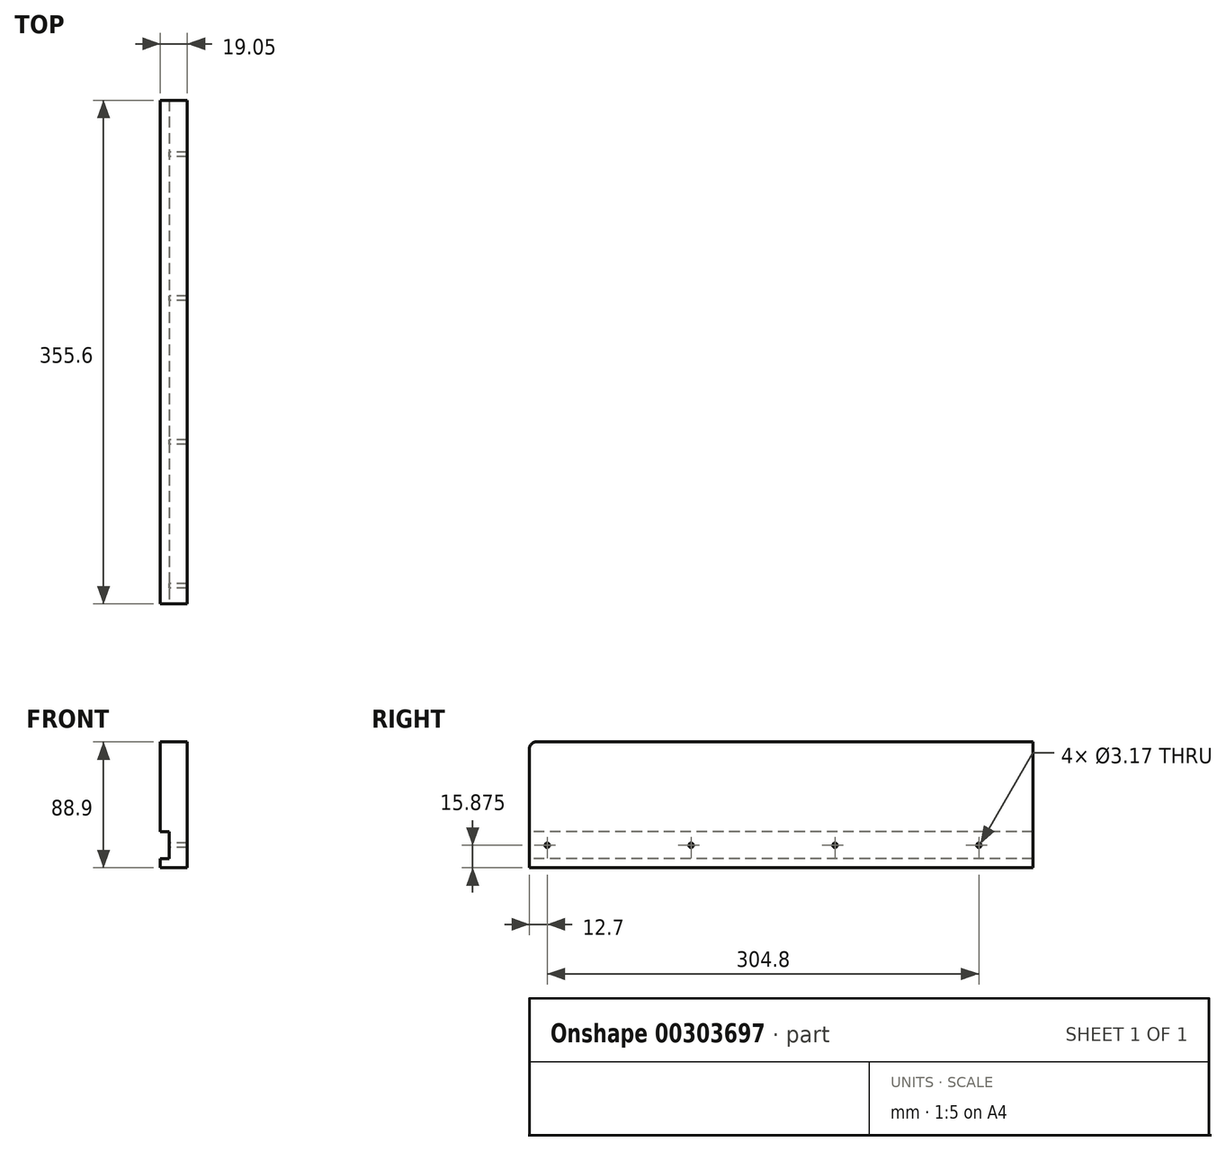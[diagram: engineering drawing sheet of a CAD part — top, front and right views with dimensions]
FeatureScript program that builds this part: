
annotation { "Feature Type Name" : "Feature", "Feature Type Description" : "" }
export const myFeature = defineFeature(function(context is Context, id is Id, definition is map)
    precondition{}
    {
        {
            var Q0;
            Q0=qCreatedBy(makeId("Right.planeOp"),FACE);
            var sketch = newSketch(context, id + "F0", { "sketchPlane" : qUnion([Q0])});
            skLineSegment(sketch, "E0.bottom", {"start": v(0, 0) * mm, "end": v(355.6, 0) * mm});
            skLineSegment(sketch, "E0.top", {"start": v(0, -88.9) * mm, "end": v(355.6, -88.9) * mm});
            skLineSegment(sketch, "E0.left", {"start": v(0, 0) * mm, "end": v(0, -88.9) * mm});
            skLineSegment(sketch, "E0.right", {"start": v(355.6, 0) * mm, "end": v(355.6, -88.9) * mm});
            skSolve(sketch);
        }
        {
            var Q0;
            Q0 = qSketchRegion(id + "F0", true);
            extrude(context, id + "F1", {"entities" : qUnion([Q0]), "depth" : 19.05 * mm});
        }
        {
            var Q0;
            Q0=makeQuery(id+"F1.opExtrude","SWEPT_EDGE",EDGE,{"disambiguationData":[OSD([sQuery(id+"F0.wireOp",EDGE,"E0.bottom"),sQuery(id+"F0.wireOp",EDGE,"E0.left")])]});
            fillet(context, id + "F2", {"entities" : qUnion([Q0]), "radius" : 5.08 * mm, "tangentPropagation" : true, "allowEdgeOverflow" : false});
        }
        {
            var Q0;
            Q0=qCreatedBy(makeId("Right.planeOp"),FACE);
            var sketch = newSketch(context, id + "F3", { "sketchPlane" : qUnion([Q0])});
            skLineSegment(sketch, "E1.bottom", {"start": v(355.6, -63.5) * mm, "end": v(0, -63.5) * mm});
            skLineSegment(sketch, "E1.top", {"start": v(355.6, -82.55) * mm, "end": v(0, -82.55) * mm});
            skLineSegment(sketch, "E1.left", {"start": v(355.6, -63.5) * mm, "end": v(355.6, -82.55) * mm});
            skLineSegment(sketch, "E1.right", {"start": v(0, -63.5) * mm, "end": v(0, -82.55) * mm});
            skSolve(sketch);
        }
        {
            var Q0;
            Q0 = qSketchRegion(id + "F3", true);
            extrude(context, id + "F4", {"entities" : qUnion([Q0]), "operationType" : NewBodyOperationType.REMOVE, "depth" : 6.35 * mm});
        }
        {
            var Q0;
            Q0=qCreatedBy(makeId("Right.planeOp"),FACE);
            var sketch = newSketch(context, id + "F5", { "sketchPlane" : qUnion([Q0])});
            skCircle(sketch, "E2", {"center": v(12.7, -73.03) * mm, "radius": 1.59 * mm});
            skCircle(sketch, "E3.1.0.0", {"center": v(114.3, -73.03) * mm, "radius": 1.59 * mm});
            skCircle(sketch, "E3.2.0.0", {"center": v(215.9, -73.03) * mm, "radius": 1.59 * mm});
            skCircle(sketch, "E3.3.0.0", {"center": v(317.5, -73.03) * mm, "radius": 1.59 * mm});
            skLineSegment(sketch, "E3.direction1", {"start": v(12.7, -73.03) * mm, "end": v(114.3, -73.03) * mm, "construction": true});
            skSolve(sketch);
        }
        {
            var Q0;
            Q0 = qSketchRegion(id + "F5", true);
            extrude(context, id + "F6", {"entities" : qUnion([Q0]), "operationType" : NewBodyOperationType.REMOVE, "endBound" : BoundingType.THROUGH_ALL, "depth" : 25.4 * mm});
        }
    });
